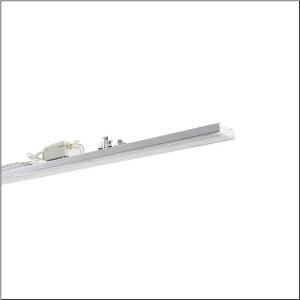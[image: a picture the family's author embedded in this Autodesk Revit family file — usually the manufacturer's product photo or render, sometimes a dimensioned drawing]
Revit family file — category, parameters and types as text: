
# Revit family: licross_r__11_recessed_mo_51te19dn495g_a71c
name_source: partatom
category: Lighting Fixtures
units: mm (PartAtom-declared; Revit-internal decimal feet)

## family parameters
Cut with Voids When Loaded = No
Host = Face
Light Source = No
Part Type = Normal
Room Calculation Point = No
Round Connector Dimension = Use Diameter
Shared = No

## types (1)
- --- (1 x LED, 9810 lm, 56.7 W, 4000K)
    Apparent Load = 57 VA
    CIE Flux Codes = 55 90 98 100 100
    Color Rendering = 80
    Color Temperature = 4000K
    Default Elevation = 1800 mm
    Description = Licross® 11 Recessed MO, luminaire insert, of sheet steel, galvanised, coil coated, white, length: 1.500mm, width: 66mm, height: 67mm, LED rated luminous flux: 9.810lm, light colour: 840, SDCM (Standard Deviation of Colour Matching)MacAdam ≤ 2 SDCM (initial), control gear: DALI 2, with plug, 5-pole, with phase selection, mains connection: 220..240V, AC, 50/60Hz, rated input power: 57W, internal wiring halogen-free, primary light control with lens, of plastic, primary optical cover: cover, of PMMA, light emission: direct distribution, primary light characteristic: double asymmetric, protection rating (complete): IP54, insulation class (complete): insulation class I (protective earthing), certification: CE, ENEC, VDE, UKCA, protection symbol: D if used in an environment with non-conductive dust loads with corresponding accessories, impact resistance: IK06, permissible ambient temperature for indoor applications: -25..+35°C, corresponds to IFS (International Featured Standards) requirements for safety and quality in the food industry, reducing of maximum allowable ambient temperature of 5°C with ceiling mounting, LABS conformity tested according to VDMA 24364:2018-05, packaging unit: 1 piece
    Height = 58 mm
    Lamp = 1 x LED
    Lamp Light Flux = 9810 lm
    Lamp Power = 56.7 W
    Lamp count = 1
    Length = 1500 mm
    Luminous efficacy = 173 lm/W
    Manufacturer = Siteco
    ModVariant = No
    Model = 51TE19DN495G
    Mounting Place = Ceiling
    Mounting Type = Pendant
    Number of Poles = 1
    OnlyDefault = Yes
    Power Factor = 1
    Product Name = Licross® 11 Recessed MO
    Product group = luminaire insert | ceiling pendant
    ProductGroupID = 901
    Protection Class = Protection class I
    Protection Degree = IP 54
    RLX_Detail_Level = 1
    RLX_Emergency_Light_Flux = 0 lm
    RLX_Emergency_Type = 0
    RLX_Emergency_Type_DB = No
    RlxData = <blob elided: 24649 chars, md5=4f612380>
    Socket = socket
    Standby Power = 0 W
    System Light Flux = 9810 lm
    System Power = 57 W
    Type Comments = factory setting: luminous flux: 100 % | dim-lin: 254 | 378 mA
    Type Image = l_1296930.jpg
    URL = http://relux.com
    VarID = @adj_106305
    Voltage = 0 V
    Weight = 0.00 kg
    Width = 66 mm

## geometry (parser evidence)
native form markers: Blend x4, Sweep x13
no freeform markers — native parametric forms only
